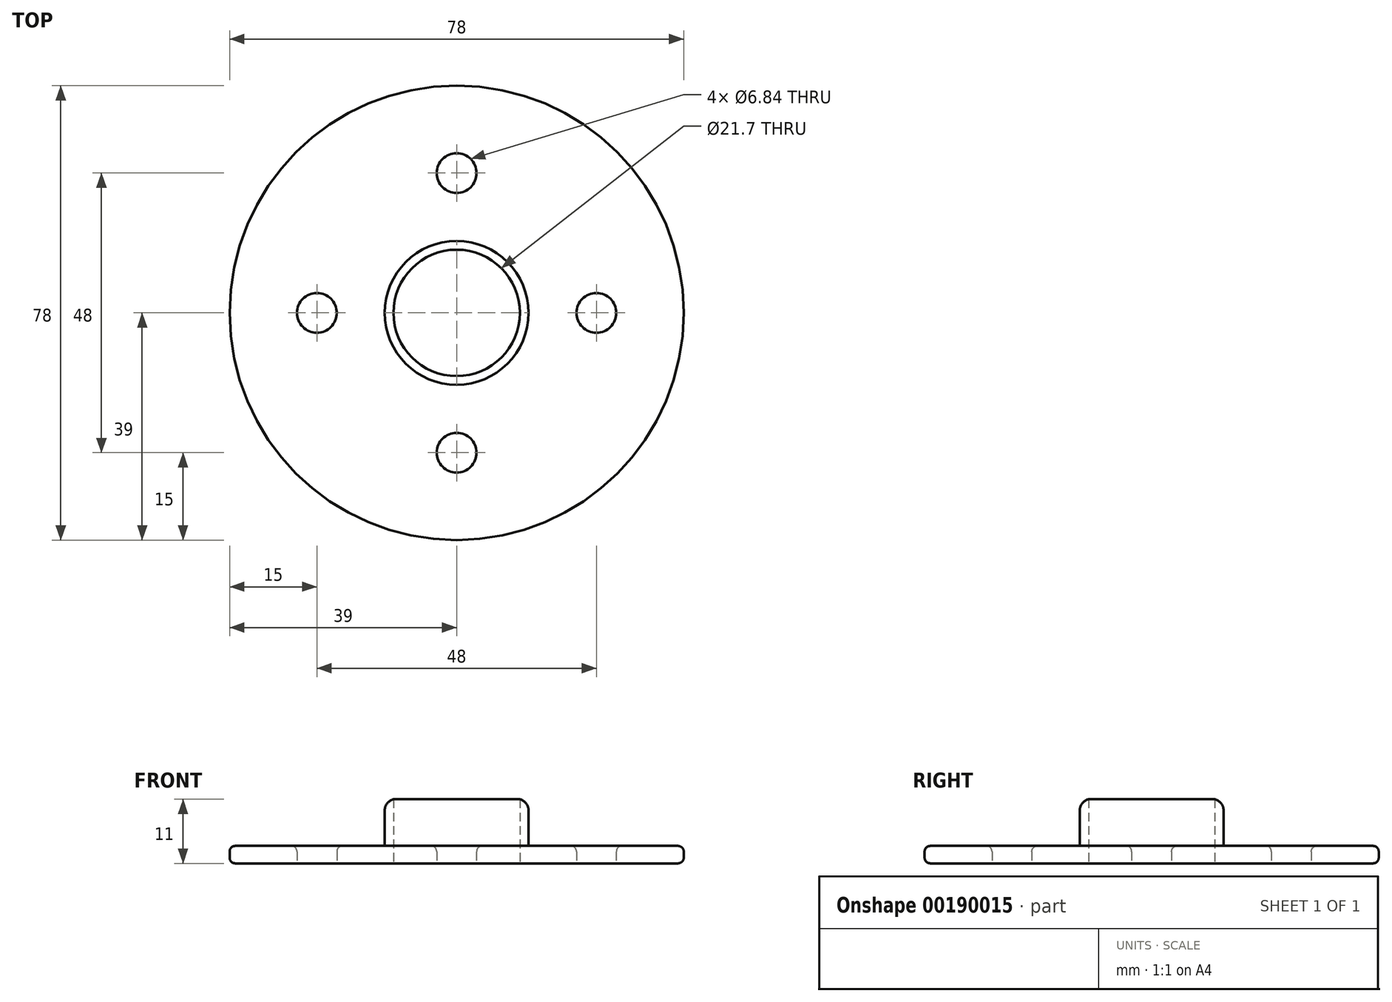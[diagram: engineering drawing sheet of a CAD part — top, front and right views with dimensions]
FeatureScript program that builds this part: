
annotation { "Feature Type Name" : "Feature", "Feature Type Description" : "" }
export const myFeature = defineFeature(function(context is Context, id is Id, definition is map)
    precondition{}
    {
        {
            var Q0;
            Q0=qCreatedBy(makeId("Top.planeOp"),FACE);
            var sketch = newSketch(context, id + "F0", { "sketchPlane" : qUnion([Q0])});
            skCircle(sketch, "E0", {"center": v(0, 0) * mm, "radius": 39 * mm});
            skLineSegment(sketch, "E1", {"start": v(0, 0) * mm, "end": v(0, 86.46) * mm});
            skCircle(sketch, "E2", {"center": v(0, 24) * mm, "radius": 3.42 * mm});
            skCircle(sketch, "E3.1.0", {"center": v(-24, 0) * mm, "radius": 3.42 * mm});
            skCircle(sketch, "E3.2.0", {"center": v(0, -24) * mm, "radius": 3.42 * mm});
            skCircle(sketch, "E3.3.0", {"center": v(24, 0) * mm, "radius": 3.42 * mm});
            skCircle(sketch, "E4", {"center": v(0, 0) * mm, "radius": 10.85 * mm});
            skSolve(sketch);
        }
        {
            var Q0;
            Q0=makeQuery(id+"F0.imprint","IMPRINT",FACE,{"disambiguationData":[TD([[makeQuery(id+"F0.imprint","IMPRINT",EDGE,{"derivedFrom":sQuery(id+"F0.wireOp",EDGE,"E0")}),1.0]])]});
            extrude(context, id + "F1", {"entities" : qUnion([Q0]), "depth" : 3 * mm});
        }
        {
            var Q0;
            Q0=makeQuery(id+"F1.opExtrude","CAP_EDGE",EDGE,{"disambiguationData":[OSD([sQuery(id+"F0.wireOp",EDGE,"E0")])],"isStart":true});
            var Q1;
            Q1=makeQuery(id+"F1.opExtrude","CAP_EDGE",EDGE,{"disambiguationData":[OSD([sQuery(id+"F0.wireOp",EDGE,"E0")])],"isStart":false});
            var Q2;
            Q2=makeQuery(id+"F1.opExtrude","CAP_EDGE",EDGE,{"disambiguationData":[OSD([sQuery(id+"F0.wireOp",EDGE,"E3.2.0")])],"isStart":false});
            var Q3;
            Q3=makeQuery(id+"F1.opExtrude","CAP_EDGE",EDGE,{"disambiguationData":[OSD([sQuery(id+"F0.wireOp",EDGE,"E3.3.0")])],"isStart":false});
            var Q4;
            Q4=makeQuery(id+"F1.opExtrude","CAP_EDGE",EDGE,{"disambiguationData":[OSD([sQuery(id+"F0.wireOp",EDGE,"E2")])],"isStart":false});
            var Q5;
            Q5=makeQuery(id+"F1.opExtrude","CAP_EDGE",EDGE,{"disambiguationData":[OSD([sQuery(id+"F0.wireOp",EDGE,"E3.1.0")])],"isStart":false});
            fillet(context, id + "F2", {"entities" : qUnion([Q0, Q1, Q2, Q3, Q4, Q5]), "radius" : 1 * mm, "tangentPropagation" : true, "allowEdgeOverflow" : false});
        }
        {
            var Q0;
            Q0=makeQuery(id+"F1.opExtrude","CAP_FACE",FACE,{"disambiguationData":[OSD([sQuery(id+"F0.wireOp",EDGE,"E0"),sQuery(id+"F0.wireOp",EDGE,"E2"),sQuery(id+"F0.wireOp",EDGE,"E3.1.0"),sQuery(id+"F0.wireOp",EDGE,"E3.2.0"),sQuery(id+"F0.wireOp",EDGE,"E3.3.0"),sQuery(id+"F0.wireOp",EDGE,"E4")])],"isStart":false});
            var sketch = newSketch(context, id + "F3", { "sketchPlane" : qUnion([Q0])});
            skCircle(sketch, "E5", {"center": v(0, 0) * mm, "radius": 12.35 * mm});
            skSolve(sketch);
        }
        {
            var Q0;
            Q0=makeQuery(id+"F3.imprint","IMPRINT",FACE,{"disambiguationData":[TD([[makeQuery(id+"F3.imprint","IMPRINT",EDGE,{"derivedFrom":sQuery(id+"F3.wireOp",EDGE,"E5")}),1.0]])]});
            extrude(context, id + "F4", {"entities" : qUnion([Q0]), "operationType" : NewBodyOperationType.ADD, "depth" : 8 * mm});
        }
        {
            var Q0;
            Q0=makeQuery(id+"F4.opExtrude","CAP_EDGE",EDGE,{"disambiguationData":[OSD([sQuery(id+"F3.wireOp",EDGE,"E5")])],"isStart":false});
            fillet(context, id + "F5", {"entities" : qUnion([Q0]), "radius" : 2 * mm, "tangentPropagation" : true, "allowEdgeOverflow" : false});
        }
    });
